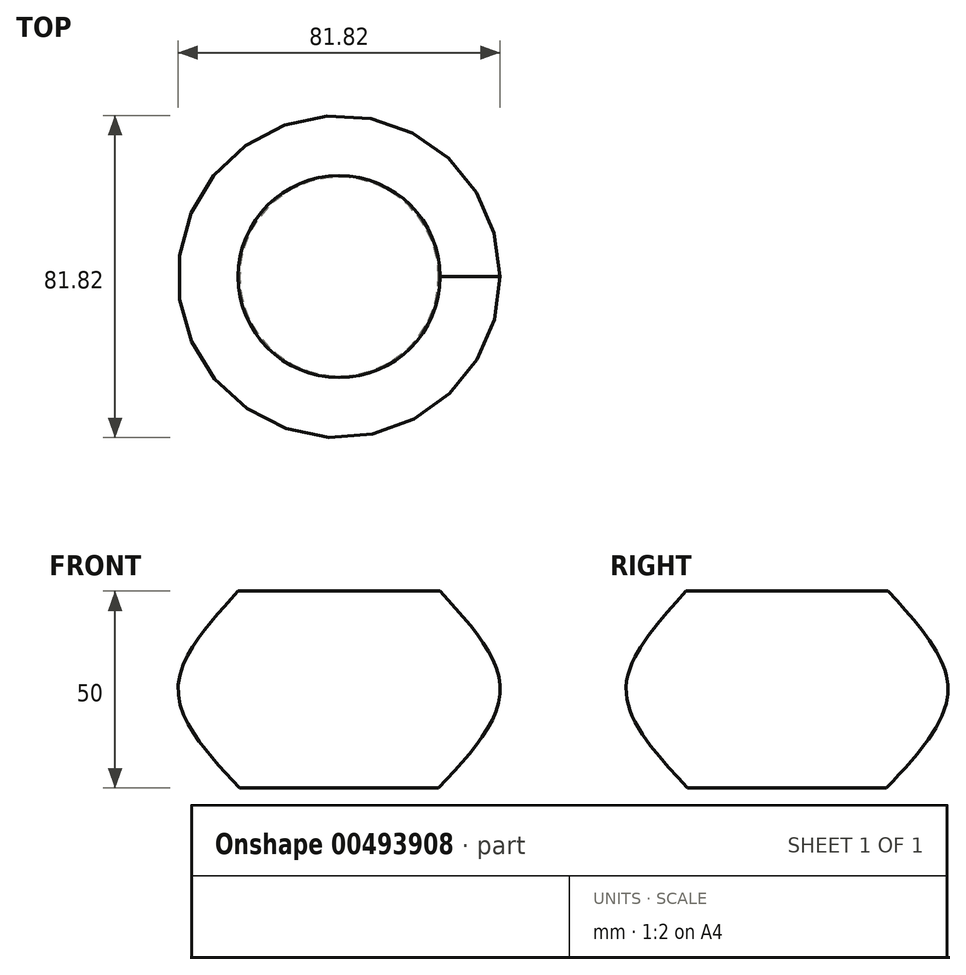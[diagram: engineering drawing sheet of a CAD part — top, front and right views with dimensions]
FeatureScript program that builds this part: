
annotation { "Feature Type Name" : "Feature", "Feature Type Description" : "" }
export const myFeature = defineFeature(function(context is Context, id is Id, definition is map)
    precondition{}
    {
        {
            var Q0;
            Q0=qCreatedBy(makeId("Top.planeOp"),FACE);
            cPlane(context, id + "F0", {"entities" : qUnion([Q0]), "cplaneType" : CPlaneType.OFFSET, "offset" : 25 * mm, "width" : 150 * mm, "height" : 150 * mm});
        }
        {
            var Q0;
            Q0=qCreatedBy(id+"F0.planeOp",FACE);
            cPlane(context, id + "F1", {"entities" : qUnion([Q0]), "cplaneType" : CPlaneType.OFFSET, "offset" : 25 * mm, "width" : 150 * mm, "height" : 150 * mm});
        }
        {
            var Q0;
            Q0=qCreatedBy(id+"F1.planeOp",FACE);
            var sketch = newSketch(context, id + "F2", { "sketchPlane" : qUnion([Q0])});
            skCircle(sketch, "E0", {"center": v(0, 0) * mm, "radius": 25.64 * mm});
            skSolve(sketch);
        }
        {
            var Q0;
            Q0=qCreatedBy(id+"F0.planeOp",FACE);
            var sketch = newSketch(context, id + "F3", { "sketchPlane" : qUnion([Q0])});
            skCircle(sketch, "E1", {"center": v(0, 0) * mm, "radius": 40.91 * mm});
            skSolve(sketch);
        }
        {
            var Q0;
            Q0=qCreatedBy(makeId("Top.planeOp"),FACE);
            var sketch = newSketch(context, id + "F4", { "sketchPlane" : qUnion([Q0])});
            skCircle(sketch, "E2", {"center": v(0, 0) * mm, "radius": 25.27 * mm});
            skSolve(sketch);
        }
        {
            var Q0;
            Q0=makeQuery(id+"F4.imprint","IMPRINT",FACE,{"disambiguationData":[TD([[makeQuery(id+"F4.imprint","IMPRINT",EDGE,{"derivedFrom":sQuery(id+"F4.wireOp",EDGE,"E2")}),1.0]])]});
            var Q1;
            Q1=makeQuery(id+"F3.imprint","IMPRINT",FACE,{"disambiguationData":[TD([[makeQuery(id+"F3.imprint","IMPRINT",EDGE,{"derivedFrom":sQuery(id+"F3.wireOp",EDGE,"E1")}),1.0]])]});
            var Q2;
            Q2=makeQuery(id+"F2.imprint","IMPRINT",FACE,{"disambiguationData":[TD([[makeQuery(id+"F2.imprint","IMPRINT",EDGE,{"derivedFrom":sQuery(id+"F2.wireOp",EDGE,"E0")}),1.0]])]});
            loft(context, id + "F5", {"sheetProfilesArray" : [{ "sheetProfileEntities" : qUnion([Q0]) }, { "sheetProfileEntities" : qUnion([Q1]) }, { "sheetProfileEntities" : qUnion([Q2]) }]});
        }
    });
